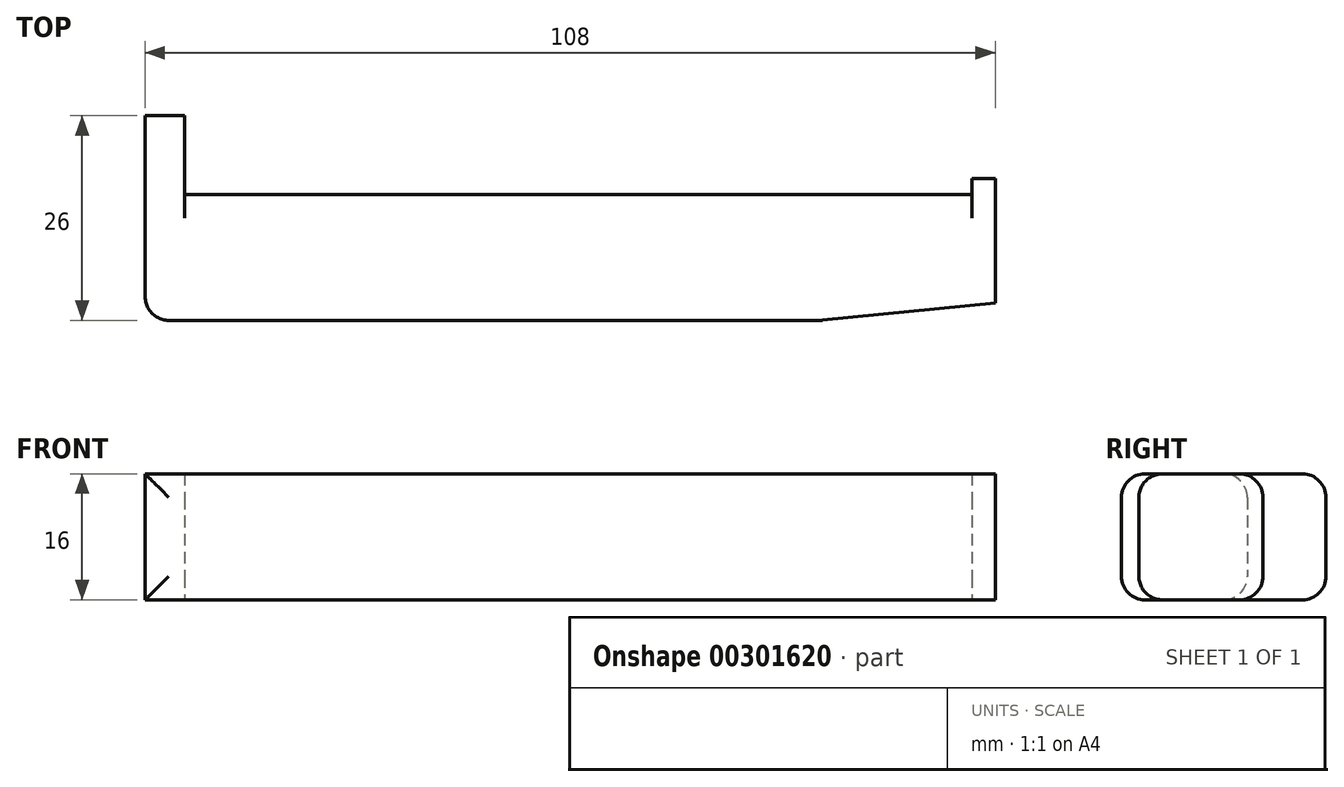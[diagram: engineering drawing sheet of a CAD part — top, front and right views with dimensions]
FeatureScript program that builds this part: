
annotation { "Feature Type Name" : "Feature", "Feature Type Description" : "" }
export const myFeature = defineFeature(function(context is Context, id is Id, definition is map)
    precondition{}
    {
        {
            var Q0;
            Q0=qCreatedBy(makeId("Right.planeOp"),FACE);
            var sketch = newSketch(context, id + "F0", { "sketchPlane" : qUnion([Q0])});
            skLineSegment(sketch, "E0.bottom", {"start": v(8, -8) * mm, "end": v(-8, -8) * mm});
            skLineSegment(sketch, "E0.top", {"start": v(8, 8) * mm, "end": v(-8, 8) * mm});
            skLineSegment(sketch, "E0.left", {"start": v(8, -8) * mm, "end": v(8, 8) * mm});
            skLineSegment(sketch, "E0.right", {"start": v(-8, -8) * mm, "end": v(-8, 8) * mm});
            skPoint(sketch, "E0.middle", {"position": v(0, 0) * mm});
            skSolve(sketch);
        }
        {
            var Q0;
            Q0=qCreatedBy(makeId("Top.planeOp"),FACE);
            var sketch = newSketch(context, id + "F1", { "sketchPlane" : qUnion([Q0])});
            skLineSegment(sketch, "E1.bottom", {"start": v(50, -8) * mm, "end": v(-50, -8) * mm});
            skLineSegment(sketch, "E1.top", {"start": v(50, 8) * mm, "end": v(-50, 8) * mm});
            skLineSegment(sketch, "E1.left", {"start": v(50, -8) * mm, "end": v(50, 8) * mm});
            skLineSegment(sketch, "E1.right", {"start": v(-50, -8) * mm, "end": v(-50, 8) * mm});
            skPoint(sketch, "E1.middle", {"position": v(0, 0) * mm});
            skLineSegment(sketch, "E2.bottom", {"start": v(50, -8) * mm, "end": v(53, -8) * mm});
            skLineSegment(sketch, "E2.top", {"start": v(50, 10) * mm, "end": v(53, 10) * mm});
            skLineSegment(sketch, "E2.left", {"start": v(50, -8) * mm, "end": v(50, 10) * mm});
            skLineSegment(sketch, "E2.right", {"start": v(53, -8) * mm, "end": v(53, 10) * mm});
            skLineSegment(sketch, "E3.bottom", {"start": v(-50, -8) * mm, "end": v(-55, -8) * mm});
            skLineSegment(sketch, "E3.top", {"start": v(-50, 18) * mm, "end": v(-55, 18) * mm});
            skLineSegment(sketch, "E3.left", {"start": v(-50, -8) * mm, "end": v(-50, 18) * mm});
            skLineSegment(sketch, "E3.right", {"start": v(-55, -8) * mm, "end": v(-55, 18) * mm});
            skLineSegment(sketch, "E4", {"start": v(50, 10) * mm, "end": v(30.1, 8) * mm, "construction": true});
            skLineSegment(sketch, "E5", {"start": v(50, 10) * mm, "end": v(52.86, -18.5) * mm, "construction": true});
            skLineSegment(sketch, "E6", {"start": v(30.9, -8) * mm, "end": v(53, -5.78) * mm});
            skSolve(sketch);
        }
        {
            var Q0;
            {var subQ3=sQuery(id+"F1.wireOp",EDGE,"E3.bottom");Q0=makeQuery(id+"F1.imprint","IMPRINT",FACE,{"disambiguationData":[TD([[makeQuery(id+"F1.imprint","IMPRINT",EDGE,{"derivedFrom":subQ3}),-1.0]])]});}
            var Q1;
            {var subQ3=sQuery(id+"F1.wireOp",EDGE,"E1.top");Q1=makeQuery(id+"F1.imprint","IMPRINT",FACE,{"disambiguationData":[TD([[makeQuery(id+"F1.imprint","IMPRINT",EDGE,{"derivedFrom":subQ3}),1.0]])]});}
            var Q2;
            {var subQ2=sQuery(id+"F1.wireOp",EDGE,"E2.top");Q2=makeQuery(id+"F1.imprint","IMPRINT",FACE,{"disambiguationData":[TD([[makeQuery(id+"F1.imprint","IMPRINT",EDGE,{"derivedFrom":subQ2}),-1.0]])]});}
            var Q3;
            Q3=sQuery(id+"F0.wireOp",VERTEX,"E0.top.end");
            var Q4;
            Q4=sQuery(id+"F0.wireOp",VERTEX,"E0.right.start");
            extrude(context, id + "F2", {"entities" : qUnion([Q0, Q1, Q2]), "endBound" : BoundingType.UP_TO_VERTEX, "endBoundEntityVertex" : qUnion([Q3]), "depth" : 25 * mm, "hasSecondDirection" : true, "secondDirectionBound" : SecondDirectionBoundingType.UP_TO_VERTEX, "secondDirectionOppositeDirection" : true, "secondDirectionBoundEntityVertex" : qUnion([Q4]), "secondDirectionDepth" : 25 * mm});
        }
        {
            var Q0;
            Q0=makeQuery(id+"F2.opExtrude","TWEAK_EDGE",EDGE,{"derivedFrom":[makeQuery(id+"F1.imprint","IMPRINT",EDGE,{"derivedFrom":sQuery(id+"F1.wireOp",EDGE,"E1.bottom")}),makeQuery(id+"F1.imprint","IMPRINT",EDGE,{"derivedFrom":sQuery(id+"F1.wireOp",EDGE,"E2.bottom")}),makeQuery(id+"F1.imprint","IMPRINT",EDGE,{"derivedFrom":sQuery(id+"F1.wireOp",EDGE,"E2.right")}),makeQuery(id+"F1.imprint","IMPRINT",EDGE,{"derivedFrom":sQuery(id+"F1.wireOp",EDGE,"E3.bottom")})]});
            var Q1;
            Q1=makeQuery(id+"F2.opExtrude","CAP_EDGE",EDGE,{"disambiguationData":[OSD([sQuery(id+"F1.wireOp",EDGE,"E1.bottom"),sQuery(id+"F1.wireOp",EDGE,"E3.bottom")])],"isStart":false});
            var Q2;
            Q2=makeQuery(id+"F2.opExtrude","SWEPT_FACE",FACE,{"disambiguationData":[OSD([sQuery(id+"F1.wireOp",EDGE,"E1.bottom"),sQuery(id+"F1.wireOp",EDGE,"E3.bottom")])]});
            var Q3;
            Q3=makeQuery(id+"F2.opExtrude","CAP_EDGE",EDGE,{"disambiguationData":[OSD([sQuery(id+"F1.wireOp",EDGE,"E3.top")])],"isStart":true});
            var Q4;
            Q4=makeQuery(id+"F2.opExtrude","CAP_EDGE",EDGE,{"disambiguationData":[OSD([sQuery(id+"F1.wireOp",EDGE,"E3.top")])],"isStart":false});
            var Q5;
            Q5=makeQuery(id+"F2.opExtrude","CAP_EDGE",EDGE,{"disambiguationData":[OSD([sQuery(id+"F1.wireOp",EDGE,"E6")])],"isStart":false});
            var Q6;
            Q6=makeQuery(id+"F2.opExtrude","CAP_EDGE",EDGE,{"disambiguationData":[OSD([sQuery(id+"F1.wireOp",EDGE,"E6")])],"isStart":true});
            var Q7;
            Q7=makeQuery(id+"F2.opExtrude","CAP_EDGE",EDGE,{"disambiguationData":[OSD([sQuery(id+"F1.wireOp",EDGE,"E1.top")])],"isStart":false});
            var Q8;
            Q8=makeQuery(id+"F2.opExtrude","CAP_EDGE",EDGE,{"disambiguationData":[OSD([sQuery(id+"F1.wireOp",EDGE,"E1.top")])],"isStart":true});
            fillet(context, id + "F3", {"entities" : qUnion([Q0, Q1, Q2, Q3, Q4, Q5, Q6, Q7, Q8]), "radius" : 3 * mm, "tangentPropagation" : true, "allowEdgeOverflow" : false});
        }
        {
            var Q0;
            Q0=makeQuery(id+"F2.opExtrude","CAP_EDGE",EDGE,{"disambiguationData":[OSD([sQuery(id+"F1.wireOp",EDGE,"E2.top")])],"isStart":false});
            var Q1;
            Q1=makeQuery(id+"F2.opExtrude","CAP_EDGE",EDGE,{"disambiguationData":[OSD([sQuery(id+"F1.wireOp",EDGE,"E2.top")])],"isStart":true});
            fillet(context, id + "F4", {"entities" : qUnion([Q0, Q1]), "radius" : 3 * mm, "tangentPropagation" : true, "allowEdgeOverflow" : false});
        }
    });
